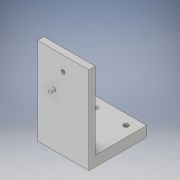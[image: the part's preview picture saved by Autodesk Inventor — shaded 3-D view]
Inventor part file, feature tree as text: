
AUTODESK INVENTOR PART (.ipt)
format: ipt  version: 2017 (Build 210142000, 142)  size: 148,992 bytes
history: native  units: in
note: dims shown in document units (in); Inventor stores cm internally (conversion verified against a paired STEP export)
features: extrude x6, sketch x6
ambient origin geometry x8: Origin, YZ Plane, XZ Plane, XY Plane, X Axis, Y Axis, Z Axis, Center Point
bodies: Solid1 (feature_tree)
feature tree (12):
  extrude  "Extrusion1"  Depth=0.15in
  extrude  "Extrusion2"  Depth=0.15in
  extrude  "Extrusion3"  Depth=0.25in TaperAngle=0.0deg
  extrude  "Extrusion4"  Depth=2.0in TaperAngle=0.0deg
  extrude  "Extrusion5"  Depth=0.4in
  extrude  "Extrusion6"  Depth=0.4in
  sketch  "Sketch1"  dims[d0=0.75in d1=0.75in d2=0.35in d3=0.15in]
  sketch  "Sketch2"  dims[d4=0.15in d5=0.15in]
  sketch  "Sketch3"  dims[d6=0.25in d7=0.0in d8=0.25in d9=0.0in]
  sketch  "Sketch4"  dims[d10=0.4in d11=2.0in d12=0.0in]
  sketch  "Sketch5"  dims[d13=0.1875in d14=0.1875in d17=0.4in]
  sketch  "Sketch6"  dims[d18=0.4in d19=0.4in d20=0.4in d21=2.0in d22=0.0in d23=0.25in d24=0.25in d25=0.0in d26=0.0in d27=0.128in d28=0.3162in d29=0.31in d30=0.165in d31=0.0in d32=2.826in d33=1.7434in d34=1.0in d35=0.0in d36=0.0in d37=3.396in]
